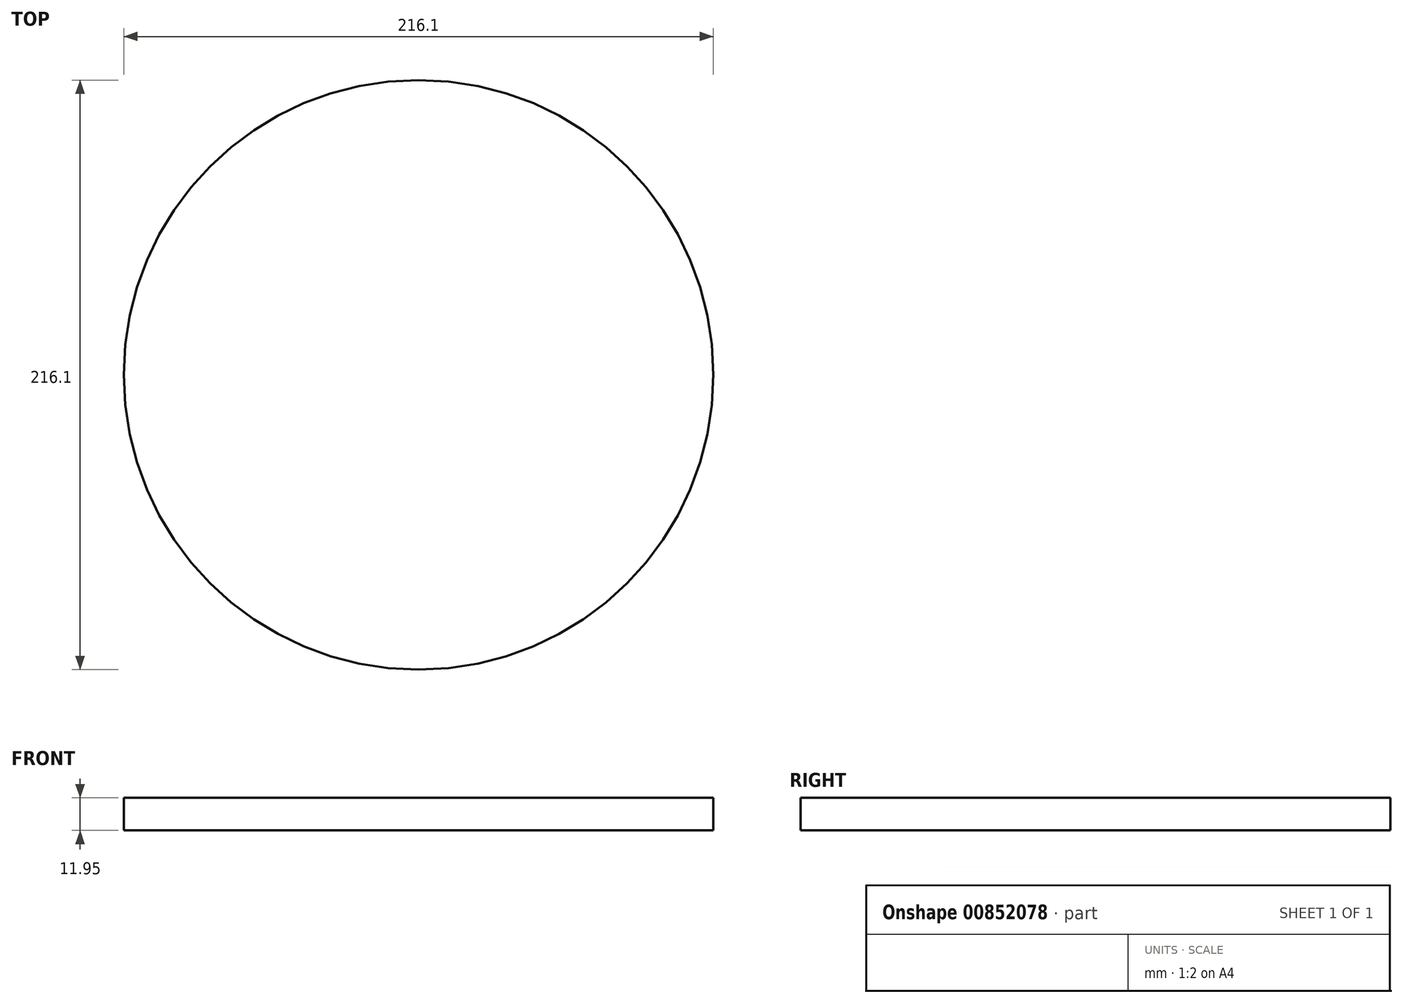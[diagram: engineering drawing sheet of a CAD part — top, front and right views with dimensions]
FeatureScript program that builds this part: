
annotation { "Feature Type Name" : "Feature", "Feature Type Description" : "" }
export const myFeature = defineFeature(function(context is Context, id is Id, definition is map)
    precondition{}
    {
        {
            var Q0;
            Q0=qCreatedBy(makeId("Top.planeOp"),FACE);
            var sketch = newSketch(context, id + "F0", { "sketchPlane" : qUnion([Q0])});
            skCircle(sketch, "E0", {"center": v(0, 0) * mm, "radius": 108.05 * mm});
            skSolve(sketch);
        }
        {
            var Q0;
            Q0 = qSketchRegion(id + "F0", true);
            var Q1;
            Q1=makeQuery(id+"F0.imprint","IMPRINT",FACE,{"disambiguationData":[TD([[makeQuery(id+"F0.imprint","IMPRINT",EDGE,{"derivedFrom":sQuery(id+"F0.wireOp",EDGE,"E0")}),1.0]])]});
            extrude(context, id + "F1", {"entities" : qUnion([Q0, Q1]), "depth" : 11.95 * mm, "offsetDistance" : 25.4 * mm});
        }
    });
